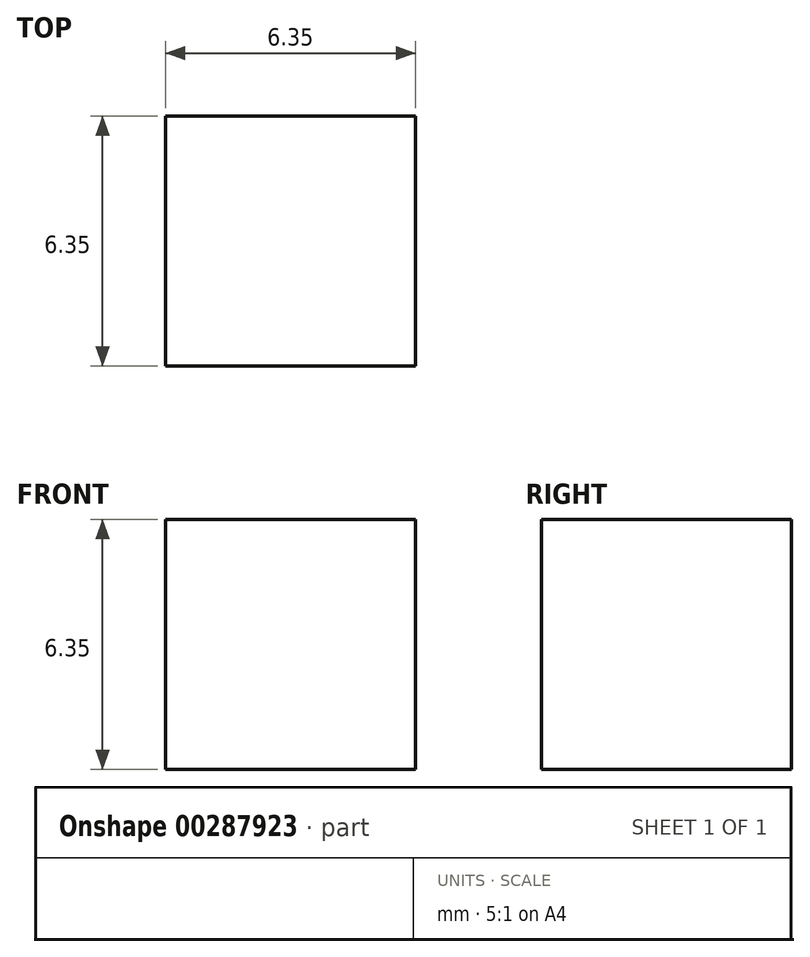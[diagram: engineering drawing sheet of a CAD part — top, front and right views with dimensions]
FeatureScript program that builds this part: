
annotation { "Feature Type Name" : "Feature", "Feature Type Description" : "" }
export const myFeature = defineFeature(function(context is Context, id is Id, definition is map)
    precondition{}
    {
        {
            var Q0;
            Q0=qCreatedBy(makeId("Top.planeOp"),FACE);
            var sketch = newSketch(context, id + "F0", { "sketchPlane" : qUnion([Q0])});
            skLineSegment(sketch, "E0.bottom", {"start": v(-119.8, -43.16) * mm, "end": v(-113.46, -43.16) * mm});
            skLineSegment(sketch, "E0.top", {"start": v(-119.8, -49.5) * mm, "end": v(-113.46, -49.5) * mm});
            skLineSegment(sketch, "E0.left", {"start": v(-119.8, -43.16) * mm, "end": v(-119.8, -49.5) * mm});
            skLineSegment(sketch, "E0.right", {"start": v(-113.46, -43.16) * mm, "end": v(-113.46, -49.5) * mm});
            skSolve(sketch);
        }
        {
            var Q0;
            Q0 = qSketchRegion(id + "F0", true);
            extrude(context, id + "F1", {"entities" : qUnion([Q0]), "depth" : 6.35 * mm, "offsetDistance" : 25.4 * mm});
        }
    });
